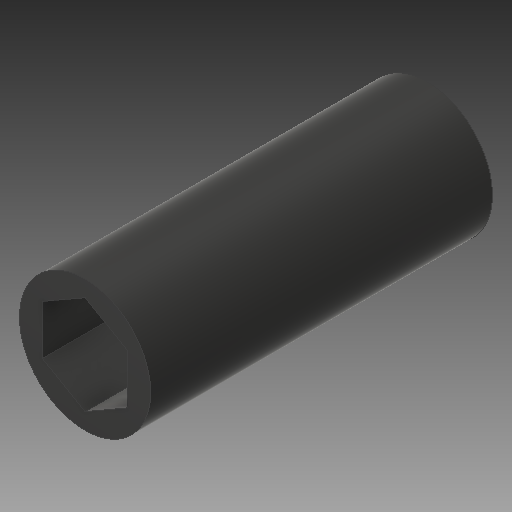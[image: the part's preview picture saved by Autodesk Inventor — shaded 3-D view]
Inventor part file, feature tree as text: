
AUTODESK INVENTOR PART (.ipt)
format: ipt  version: 2017 (Build 210142000, 142)  size: 108,544 bytes
history: native  units: in
note: dims shown in document units (in); Inventor stores cm internally (conversion verified against a paired STEP export)
features: extrude x1, sketch x1
ambient origin geometry x8: Origin, YZ Plane, XZ Plane, XY Plane, X Axis, Y Axis, Z Axis, Center Point
bodies: Solid1 (feature_tree)
feature tree (2):
  extrude  "Extrusion1"  Depth=2.0in
  sketch  "Sketch1"  dims[d0=0.5in d1=0.768in d2=2.0in d3=0.0in]
